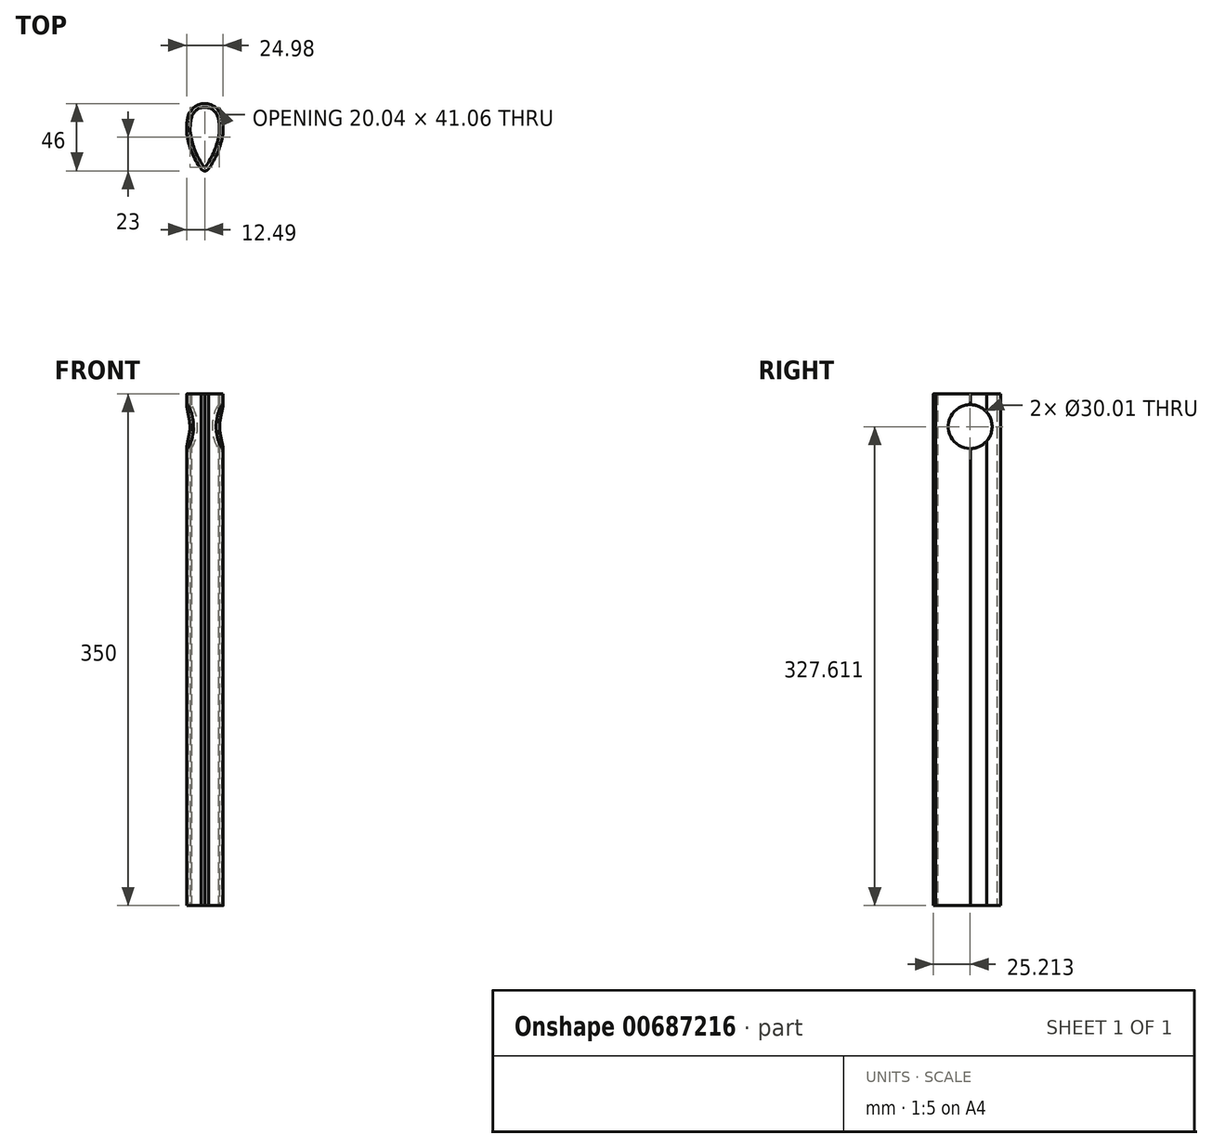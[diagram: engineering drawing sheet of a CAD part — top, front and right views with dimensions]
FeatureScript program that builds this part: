
annotation { "Feature Type Name" : "Feature", "Feature Type Description" : "" }
export const myFeature = defineFeature(function(context is Context, id is Id, definition is map)
    precondition{}
    {
        {
            var Q0;
            Q0=qCreatedBy(makeId("Top.planeOp"),FACE);
            var sketch = newSketch(context, id + "F0", { "sketchPlane" : qUnion([Q0])});
            skArc(sketch, "E0", {"start": v(0, 23) * mm, "mid": v(-7.48, 20.33) * mm, "end": v(-11.6, 13.53) * mm});
            skArc(sketch, "E1", {"start": v(-11.6, 13.53) * mm, "mid": v(-12.41, 7.92) * mm, "end": v(-12.34, 2.25) * mm});
            skArc(sketch, "E2", {"start": v(-12.34, 2.25) * mm, "mid": v(-8.87, -10.23) * mm, "end": v(-2.58, -21.55) * mm});
            skArc(sketch, "E3", {"start": v(-2.58, -21.55) * mm, "mid": v(-1.48, -22.62) * mm, "end": v(0, -23) * mm});
            skArc(sketch, "E4", {"start": v(0, -23) * mm, "mid": v(1.48, -22.62) * mm, "end": v(2.58, -21.55) * mm});
            skArc(sketch, "E5", {"start": v(2.58, -21.55) * mm, "mid": v(8.87, -10.23) * mm, "end": v(12.34, 2.25) * mm});
            skArc(sketch, "E6", {"start": v(12.34, 2.25) * mm, "mid": v(12.41, 7.92) * mm, "end": v(11.6, 13.53) * mm});
            skArc(sketch, "E7", {"start": v(11.6, 13.53) * mm, "mid": v(7.48, 20.33) * mm, "end": v(0, 23) * mm});
            skArc(sketch, "E8.0", {"start": v(9.18, 13.01) * mm, "mid": v(5.93, 18.41) * mm, "end": v(0, 20.53) * mm});
            skArc(sketch, "E8.1", {"start": v(9.89, 2.56) * mm, "mid": v(9.95, 7.81) * mm, "end": v(9.18, 13.01) * mm});
            skArc(sketch, "E8.2", {"start": v(0, 20.53) * mm, "mid": v(-5.93, 18.41) * mm, "end": v(-9.18, 13.01) * mm});
            skArc(sketch, "E8.3", {"start": v(0.5, -20.23) * mm, "mid": v(6.54, -9.4) * mm, "end": v(9.89, 2.56) * mm});
            skArc(sketch, "E8.4", {"start": v(-9.18, 13.01) * mm, "mid": v(-9.95, 7.81) * mm, "end": v(-9.89, 2.56) * mm});
            skArc(sketch, "E8.5", {"start": v(-9.89, 2.56) * mm, "mid": v(-6.54, -9.4) * mm, "end": v(-0.5, -20.23) * mm});
            skArc(sketch, "E8.6", {"start": v(-0.5, -20.23) * mm, "mid": v(-0.3, -20.45) * mm, "end": v(0, -20.53) * mm});
            skArc(sketch, "E8.7", {"start": v(0, -20.53) * mm, "mid": v(0.3, -20.45) * mm, "end": v(0.5, -20.23) * mm});
            skSolve(sketch);
        }
        {
            var Q0;
            Q0=makeQuery(id+"F0.imprint","IMPRINT",FACE,{"disambiguationData":[TD([[makeQuery(id+"F0.imprint","IMPRINT",EDGE,{"derivedFrom":sQuery(id+"F0.wireOp",EDGE,"E0")}),1.0]])]});
            extrude(context, id + "F1", {"entities" : qUnion([Q0]), "depth" : 50 * mm, "offsetDistance" : 25 * mm});
        }
        {
            var Q0;
            Q0=qCreatedBy(makeId("Right.planeOp"),FACE);
            var sketch = newSketch(context, id + "F2", { "sketchPlane" : qUnion([Q0])});
            skCircle(sketch, "E9", {"center": v(2.21, 27.61) * mm, "radius": 15 * mm});
            skSolve(sketch);
        }
        {
            var Q0;
            Q0 = qSketchRegion(id + "F2", true);
            extrude(context, id + "F3", {"entities" : qUnion([Q0]), "operationType" : NewBodyOperationType.REMOVE, "endBound" : BoundingType.SYMMETRIC, "depth" : 50 * mm, "offsetDistance" : 25 * mm});
        }
        {
            var Q0;
            Q0=makeQuery(id+"F1.opExtrude","CAP_FACE",FACE,{"disambiguationData":[OSD([sQuery(id+"F0.wireOp",EDGE,"E0"),sQuery(id+"F0.wireOp",EDGE,"E1"),sQuery(id+"F0.wireOp",EDGE,"E2"),sQuery(id+"F0.wireOp",EDGE,"E3"),sQuery(id+"F0.wireOp",EDGE,"E4"),sQuery(id+"F0.wireOp",EDGE,"E5"),sQuery(id+"F0.wireOp",EDGE,"E6"),sQuery(id+"F0.wireOp",EDGE,"E7"),sQuery(id+"F0.wireOp",EDGE,"E8.0"),sQuery(id+"F0.wireOp",EDGE,"E8.1"),sQuery(id+"F0.wireOp",EDGE,"E8.2"),sQuery(id+"F0.wireOp",EDGE,"E8.3"),sQuery(id+"F0.wireOp",EDGE,"E8.4"),sQuery(id+"F0.wireOp",EDGE,"E8.5"),sQuery(id+"F0.wireOp",EDGE,"E8.6"),sQuery(id+"F0.wireOp",EDGE,"E8.7")])],"isStart":true});
            extrude(context, id + "F4", {"entities" : qUnion([Q0]), "operationType" : NewBodyOperationType.ADD, "depth" : 300 * mm, "offsetDistance" : 25 * mm});
        }
    });
